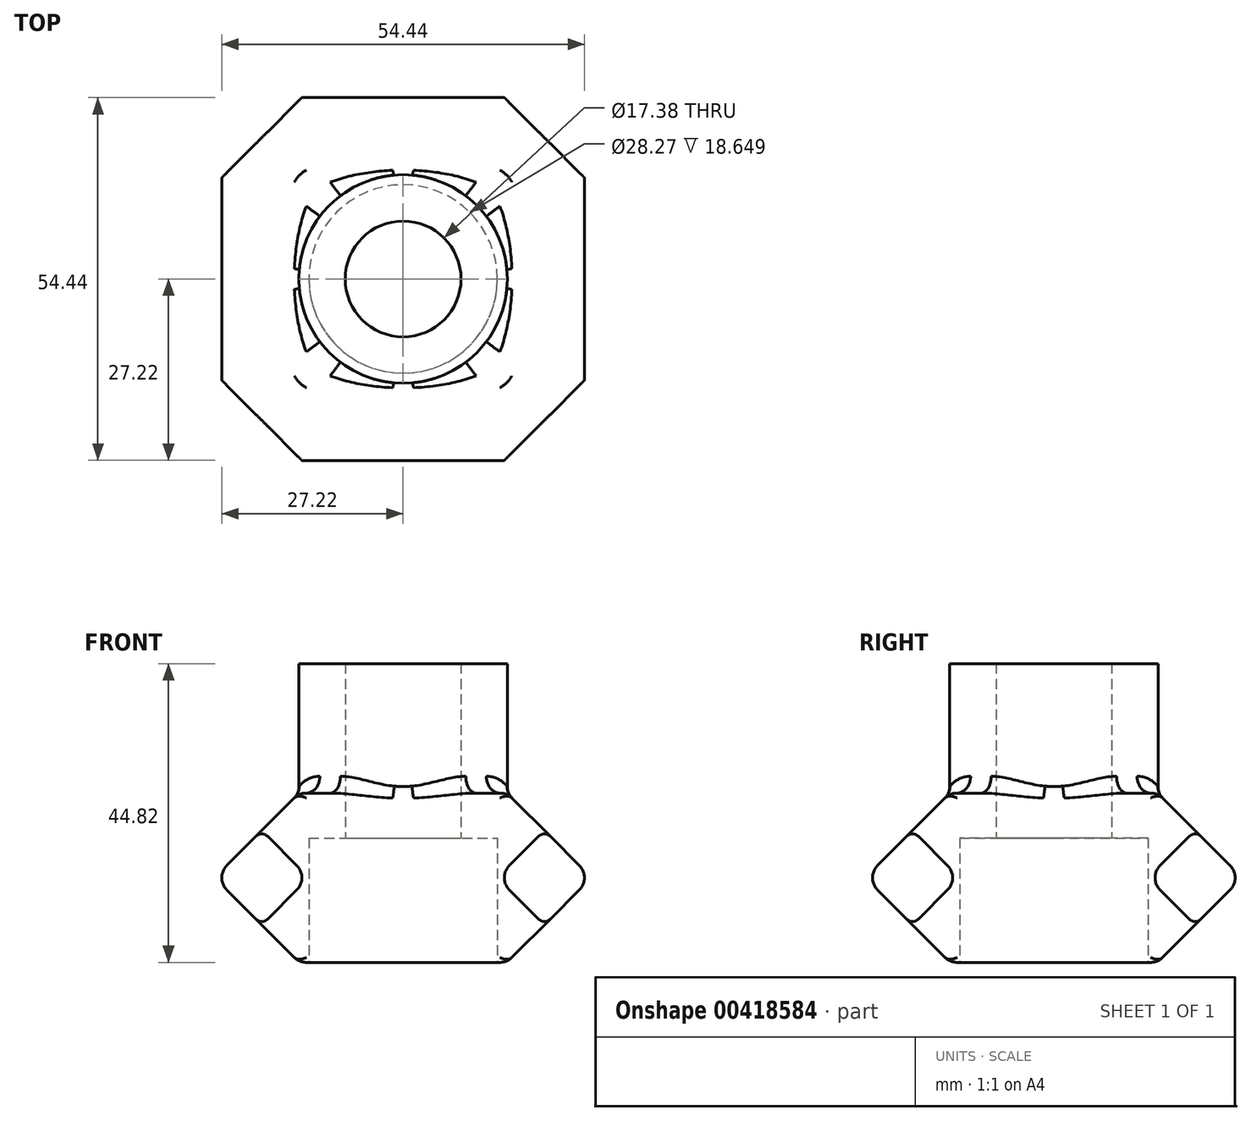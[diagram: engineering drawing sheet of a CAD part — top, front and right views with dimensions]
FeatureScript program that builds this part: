
annotation { "Feature Type Name" : "Feature", "Feature Type Description" : "" }
export const myFeature = defineFeature(function(context is Context, id is Id, definition is map)
    precondition{}
    {
        {
            var Q0;
            Q0=qCreatedBy(makeId("Front.planeOp"),FACE);
            var sketch = newSketch(context, id + "F0", { "sketchPlane" : qUnion([Q0])});
            skLineSegment(sketch, "E0", {"start": v(0, 0) * mm, "end": v(0, 44.82) * mm, "construction": true});
            skLineSegment(sketch, "E1", {"start": v(0, 44.82) * mm, "end": v(15.64, 44.82) * mm, "construction": true});
            skLineSegment(sketch, "E2", {"start": v(15.64, 44.82) * mm, "end": v(15.64, 18.65) * mm});
            skLineSegment(sketch, "E3", {"start": v(8.69, 44.82) * mm, "end": v(8.69, 18.65) * mm});
            skLineSegment(sketch, "E4", {"start": v(8.69, 44.82) * mm, "end": v(15.64, 44.82) * mm});
            skPoint(sketch, "E5.orphan", {"position": v(8.69, 7) * mm});
            skLineSegment(sketch, "E6", {"start": v(8.69, 18.65) * mm, "end": v(15.64, 18.65) * mm});
            skSolve(sketch);
        }
        {
            var Q0;
            {var subQ0=sQuery(id+"F0.wireOp",EDGE,"E2");Q0=makeQuery(id+"F0.imprint","IMPRINT",FACE,{"disambiguationData":[TD([[makeQuery(id+"F0.imprint","IMPRINT",EDGE,{"derivedFrom":subQ0}),-1.0]])]});}
            var Q1;
            Q1=sQuery(id+"F0.wireOp",EDGE,"E0");
            revolve(context, id + "F1", {"entities" : qUnion([Q0]), "axis" : qUnion([Q1]), "revolveType" : RevolveType.FULL});
        }
        {
            var Q0;
            Q0=qCreatedBy(makeId("Top.planeOp"),FACE);
            var sketch = newSketch(context, id + "F2", { "sketchPlane" : qUnion([Q0])});
            skLineSegment(sketch, "E7", {"start": v(0, 0) * mm, "end": v(28.27, 0) * mm, "construction": true});
            skLineSegment(sketch, "E8", {"start": v(0, 0) * mm, "end": v(0, 28.27) * mm, "construction": true});
            skLineSegment(sketch, "E9", {"start": v(0, 0) * mm, "end": v(-28.27, 0) * mm, "construction": true});
            skLineSegment(sketch, "E10", {"start": v(0, 0) * mm, "end": v(0, -28.27) * mm, "construction": true});
            skLineSegment(sketch, "E11", {"start": v(14.14, 0) * mm, "end": v(14.14, -28.27) * mm});
            skLineSegment(sketch, "E12", {"start": v(0, -14.14) * mm, "end": v(28.27, -14.14) * mm});
            skLineSegment(sketch, "E13", {"start": v(-14.14, 0) * mm, "end": v(-14.14, -28.27) * mm});
            skPoint(sketch, "E13.endSnap0", {"position": v(-14.14, 0) * mm});
            skLineSegment(sketch, "E14", {"start": v(-14.14, 0) * mm, "end": v(-14.14, 28.27) * mm});
            skLineSegment(sketch, "E15", {"start": v(14.14, 0) * mm, "end": v(14.14, 28.27) * mm});
            skLineSegment(sketch, "E16", {"start": v(0, 14.14) * mm, "end": v(28.27, 14.14) * mm});
            skLineSegment(sketch, "E17", {"start": v(0, 14.14) * mm, "end": v(-28.27, 14.14) * mm});
            skLineSegment(sketch, "E18", {"start": v(0, -14.14) * mm, "end": v(-28.27, -14.14) * mm});
            skLineSegment(sketch, "E19", {"start": v(28.27, 14.14) * mm, "end": v(28.27, -14.14) * mm});
            skLineSegment(sketch, "E20", {"start": v(14.14, 28.27) * mm, "end": v(-14.14, 28.27) * mm});
            skLineSegment(sketch, "E21", {"start": v(-28.27, 14.14) * mm, "end": v(-28.27, -14.14) * mm});
            skLineSegment(sketch, "E22", {"start": v(-14.14, -28.27) * mm, "end": v(14.14, -28.27) * mm});
            skLineSegment(sketch, "E23", {"start": v(14.14, -28.27) * mm, "end": v(28.27, -14.14) * mm});
            skLineSegment(sketch, "E24", {"start": v(14.14, 28.27) * mm, "end": v(28.27, 14.14) * mm});
            skLineSegment(sketch, "E25", {"start": v(-14.14, 28.27) * mm, "end": v(-28.27, 14.14) * mm});
            skLineSegment(sketch, "E26", {"start": v(-28.27, -14.14) * mm, "end": v(-14.14, -28.27) * mm});
            skCircle(sketch, "E27", {"center": v(0, 0) * mm, "radius": 14.14 * mm});
            skSolve(sketch);
        }
        {
            var Q0;
            {var subQ0=sQuery(id+"F2.wireOp",EDGE,"E26");Q0=makeQuery(id+"F2.imprint","IMPRINT",FACE,{"disambiguationData":[TD([[makeQuery(id+"F2.imprint","IMPRINT",EDGE,{"derivedFrom":subQ0}),1.0]])]});}
            var Q1;
            {var subQ0=sQuery(id+"F2.wireOp",EDGE,"E23");Q1=makeQuery(id+"F2.imprint","IMPRINT",FACE,{"disambiguationData":[TD([[makeQuery(id+"F2.imprint","IMPRINT",EDGE,{"derivedFrom":subQ0}),1.0]])]});}
            var Q2;
            {var subQ0=sQuery(id+"F2.wireOp",EDGE,"E19");Q2=makeQuery(id+"F2.imprint","IMPRINT",FACE,{"disambiguationData":[TD([[makeQuery(id+"F2.imprint","IMPRINT",EDGE,{"derivedFrom":subQ0}),-1.0]])]});}
            var Q3;
            {var subQ5=sQuery(id+"F2.wireOp",EDGE,"E20");Q3=makeQuery(id+"F2.imprint","IMPRINT",FACE,{"disambiguationData":[TD([[makeQuery(id+"F2.imprint","IMPRINT",EDGE,{"derivedFrom":subQ5}),1.0]])]});}
            var Q4;
            {var subQ0=sQuery(id+"F2.wireOp",EDGE,"E25");Q4=makeQuery(id+"F2.imprint","IMPRINT",FACE,{"disambiguationData":[TD([[makeQuery(id+"F2.imprint","IMPRINT",EDGE,{"derivedFrom":subQ0}),1.0]])]});}
            var Q5;
            {var subQ0=sQuery(id+"F2.wireOp",EDGE,"E24");Q5=makeQuery(id+"F2.imprint","IMPRINT",FACE,{"disambiguationData":[TD([[makeQuery(id+"F2.imprint","IMPRINT",EDGE,{"derivedFrom":subQ0}),-1.0]])]});}
            var Q6;
            {var subQ0=sQuery(id+"F2.wireOp",EDGE,"E21");Q6=makeQuery(id+"F2.imprint","IMPRINT",FACE,{"disambiguationData":[TD([[makeQuery(id+"F2.imprint","IMPRINT",EDGE,{"derivedFrom":subQ0}),1.0]])]});}
            var Q7;
            {var subQ1=sQuery(id+"F2.wireOp",EDGE,"E14");var subQ3=sQuery(id+"F2.wireOp",EDGE,"E17");var subQ4=makeQuery(id+"F2.imprint","INTERSECT",VERTEX,{"derivedFrom":[subQ1,subQ3]});Q7=makeQuery(id+"F2.imprint","IMPRINT",FACE,{"disambiguationData":[TD([[makeQuery(id+"F2.imprint","IMPRINT",EDGE,{"disambiguationData":[TD([[subQ4,1.0]])],"derivedFrom":subQ1}),-1.0]])]});}
            var Q8;
            {var subQ1=sQuery(id+"F2.wireOp",EDGE,"E15");var subQ3=sQuery(id+"F2.wireOp",EDGE,"E16");var subQ4=makeQuery(id+"F2.imprint","INTERSECT",VERTEX,{"derivedFrom":[subQ1,subQ3]});Q8=makeQuery(id+"F2.imprint","IMPRINT",FACE,{"disambiguationData":[TD([[makeQuery(id+"F2.imprint","IMPRINT",EDGE,{"disambiguationData":[TD([[subQ4,1.0]])],"derivedFrom":subQ1}),1.0]])]});}
            var Q9;
            {var subQ1=sQuery(id+"F2.wireOp",EDGE,"E11");var subQ3=sQuery(id+"F2.wireOp",EDGE,"E12");var subQ4=makeQuery(id+"F2.imprint","INTERSECT",VERTEX,{"derivedFrom":[subQ1,subQ3]});Q9=makeQuery(id+"F2.imprint","IMPRINT",FACE,{"disambiguationData":[TD([[makeQuery(id+"F2.imprint","IMPRINT",EDGE,{"disambiguationData":[TD([[subQ4,1.0]])],"derivedFrom":subQ1}),-1.0]])]});}
            var Q10;
            {var subQ1=sQuery(id+"F2.wireOp",EDGE,"E13");var subQ3=sQuery(id+"F2.wireOp",EDGE,"E18");var subQ4=makeQuery(id+"F2.imprint","INTERSECT",VERTEX,{"derivedFrom":[subQ1,subQ3]});Q10=makeQuery(id+"F2.imprint","IMPRINT",FACE,{"disambiguationData":[TD([[makeQuery(id+"F2.imprint","IMPRINT",EDGE,{"disambiguationData":[TD([[subQ4,1.0]])],"derivedFrom":subQ1}),1.0]])]});}
            var Q11;
            {var subQ5=sQuery(id+"F2.wireOp",EDGE,"E22");Q11=makeQuery(id+"F2.imprint","IMPRINT",FACE,{"disambiguationData":[TD([[makeQuery(id+"F2.imprint","IMPRINT",EDGE,{"derivedFrom":subQ5}),1.0]])]});}
            extrude(context, id + "F3", {"entities" : qUnion([Q0, Q1, Q2, Q3, Q4, Q5, Q6, Q7, Q8, Q9, Q10, Q11]), "operationType" : NewBodyOperationType.ADD, "depth" : 25.4 * mm});
        }
        {
            var Q0;
            Q0=makeQuery(id+"F3.opExtrude","CAP_EDGE",EDGE,{"disambiguationData":[OSD([sQuery(id+"F2.wireOp",EDGE,"E26")])],"isStart":false});
            var Q1;
            Q1=makeQuery(id+"F3.opExtrude","CAP_EDGE",EDGE,{"disambiguationData":[OSD([sQuery(id+"F2.wireOp",EDGE,"E26")])],"isStart":true});
            var Q2;
            Q2=makeQuery(id+"F3.opExtrude","CAP_EDGE",EDGE,{"disambiguationData":[OSD([sQuery(id+"F2.wireOp",EDGE,"E23")])],"isStart":true});
            var Q3;
            Q3=makeQuery(id+"F3.opExtrude","CAP_EDGE",EDGE,{"disambiguationData":[OSD([sQuery(id+"F2.wireOp",EDGE,"E23")])],"isStart":false});
            var Q4;
            Q4=makeQuery(id+"F3.opExtrude","CAP_EDGE",EDGE,{"disambiguationData":[OSD([sQuery(id+"F2.wireOp",EDGE,"E24")])],"isStart":false});
            var Q5;
            Q5=makeQuery(id+"F3.opExtrude","CAP_EDGE",EDGE,{"disambiguationData":[OSD([sQuery(id+"F2.wireOp",EDGE,"E24")])],"isStart":true});
            var Q6;
            Q6=makeQuery(id+"F3.opExtrude","CAP_EDGE",EDGE,{"disambiguationData":[OSD([sQuery(id+"F2.wireOp",EDGE,"E25")])],"isStart":true});
            var Q7;
            Q7=makeQuery(id+"F3.opExtrude","CAP_EDGE",EDGE,{"disambiguationData":[OSD([sQuery(id+"F2.wireOp",EDGE,"E25")])],"isStart":false});
            chamfer(context, id + "F4", {"entities" : qUnion([Q0, Q1, Q2, Q3, Q4, Q5, Q6, Q7]), "width" : 5.08 * mm, "tangentPropagation" : true});
        }
        {
            var Q0;
            Q0=makeQuery(id+"F3.opExtrude","CAP_EDGE",EDGE,{"disambiguationData":[OSD([sQuery(id+"F2.wireOp",EDGE,"E20")])],"isStart":false});
            var Q1;
            Q1=makeQuery(id+"F3.opExtrude","CAP_EDGE",EDGE,{"disambiguationData":[OSD([sQuery(id+"F2.wireOp",EDGE,"E20")])],"isStart":true});
            var Q2;
            Q2=makeQuery(id+"F3.opExtrude","CAP_EDGE",EDGE,{"disambiguationData":[OSD([sQuery(id+"F2.wireOp",EDGE,"E21")])],"isStart":true});
            var Q3;
            Q3=makeQuery(id+"F3.opExtrude","CAP_EDGE",EDGE,{"disambiguationData":[OSD([sQuery(id+"F2.wireOp",EDGE,"E21")])],"isStart":false});
            var Q4;
            Q4=makeQuery(id+"F3.opExtrude","CAP_EDGE",EDGE,{"disambiguationData":[OSD([sQuery(id+"F2.wireOp",EDGE,"E22")])],"isStart":false});
            var Q5;
            Q5=makeQuery(id+"F3.opExtrude","CAP_EDGE",EDGE,{"disambiguationData":[OSD([sQuery(id+"F2.wireOp",EDGE,"E22")])],"isStart":true});
            var Q6;
            Q6=makeQuery(id+"F3.opExtrude","CAP_EDGE",EDGE,{"disambiguationData":[OSD([sQuery(id+"F2.wireOp",EDGE,"E19")])],"isStart":false});
            var Q7;
            Q7=makeQuery(id+"F3.opExtrude","CAP_EDGE",EDGE,{"disambiguationData":[OSD([sQuery(id+"F2.wireOp",EDGE,"E19")])],"isStart":true});
            chamfer(context, id + "F5", {"entities" : qUnion([Q0, Q1, Q2, Q3, Q4, Q5, Q6, Q7]), "width" : 12.7 * mm, "tangentPropagation" : true});
        }
        {
            var Q0;
            Q0=makeQuery(id+"F5.opChamfer","BLEND_EDGE",EDGE,{"blendedFrom":[makeQuery(id+"F3.opExtrude","CAP_EDGE",EDGE,{"disambiguationData":[OSD([sQuery(id+"F2.wireOp",EDGE,"E20")])],"isStart":false}),makeQuery(id+"F3.opExtrude","CAP_EDGE",EDGE,{"disambiguationData":[OSD([sQuery(id+"F2.wireOp",EDGE,"E21")])],"isStart":false})],"blendedInto":[]});
            var Q1;
            {var subQ0=sQuery(id+"F2.wireOp",EDGE,"E21");Q1=makeQuery(id+"F5.opChamfer","BLEND_EDGE",EDGE,{"disambiguationData":[OD(0.0)],"blendedFrom":[makeQuery(id+"F3.opExtrude","CAP_EDGE",EDGE,{"disambiguationData":[OSD([subQ0])],"isStart":false}),makeQuery(id+"F3.opExtrude","CAP_FACE",FACE,{"disambiguationData":[OSD([sQuery(id+"F2.wireOp",EDGE,"E19"),sQuery(id+"F2.wireOp",EDGE,"E20"),subQ0,sQuery(id+"F2.wireOp",EDGE,"E22"),sQuery(id+"F2.wireOp",EDGE,"E23"),sQuery(id+"F2.wireOp",EDGE,"E24"),sQuery(id+"F2.wireOp",EDGE,"E25"),sQuery(id+"F2.wireOp",EDGE,"E26"),sQuery(id+"F2.wireOp",EDGE,"E27")])],"isStart":false})],"blendedInto":[makeQuery(id+"F3.opExtrude","CAP_FACE",FACE,{"disambiguationData":[OSD([sQuery(id+"F2.wireOp",EDGE,"E19"),sQuery(id+"F2.wireOp",EDGE,"E20"),subQ0,sQuery(id+"F2.wireOp",EDGE,"E22"),sQuery(id+"F2.wireOp",EDGE,"E23"),sQuery(id+"F2.wireOp",EDGE,"E24"),sQuery(id+"F2.wireOp",EDGE,"E25"),sQuery(id+"F2.wireOp",EDGE,"E26"),sQuery(id+"F2.wireOp",EDGE,"E27")])],"isStart":false})]});}
            var Q2;
            {var subQ0=sQuery(id+"F2.wireOp",EDGE,"E20");Q2=makeQuery(id+"F5.opChamfer","BLEND_EDGE",EDGE,{"disambiguationData":[OD(1.0)],"blendedFrom":[makeQuery(id+"F3.opExtrude","CAP_EDGE",EDGE,{"disambiguationData":[OSD([subQ0])],"isStart":false}),makeQuery(id+"F3.opExtrude","CAP_FACE",FACE,{"disambiguationData":[OSD([sQuery(id+"F2.wireOp",EDGE,"E19"),subQ0,sQuery(id+"F2.wireOp",EDGE,"E21"),sQuery(id+"F2.wireOp",EDGE,"E22"),sQuery(id+"F2.wireOp",EDGE,"E23"),sQuery(id+"F2.wireOp",EDGE,"E24"),sQuery(id+"F2.wireOp",EDGE,"E25"),sQuery(id+"F2.wireOp",EDGE,"E26"),sQuery(id+"F2.wireOp",EDGE,"E27")])],"isStart":false})],"blendedInto":[makeQuery(id+"F3.opExtrude","CAP_FACE",FACE,{"disambiguationData":[OSD([sQuery(id+"F2.wireOp",EDGE,"E19"),subQ0,sQuery(id+"F2.wireOp",EDGE,"E21"),sQuery(id+"F2.wireOp",EDGE,"E22"),sQuery(id+"F2.wireOp",EDGE,"E23"),sQuery(id+"F2.wireOp",EDGE,"E24"),sQuery(id+"F2.wireOp",EDGE,"E25"),sQuery(id+"F2.wireOp",EDGE,"E26"),sQuery(id+"F2.wireOp",EDGE,"E27")])],"isStart":false})]});}
            var Q3;
            {var subQ0=sQuery(id+"F2.wireOp",EDGE,"E19");Q3=makeQuery(id+"F5.opChamfer","BLEND_EDGE",EDGE,{"disambiguationData":[OD(0.0)],"blendedFrom":[makeQuery(id+"F3.opExtrude","CAP_EDGE",EDGE,{"disambiguationData":[OSD([subQ0])],"isStart":false}),makeQuery(id+"F3.opExtrude","CAP_FACE",FACE,{"disambiguationData":[OSD([subQ0,sQuery(id+"F2.wireOp",EDGE,"E20"),sQuery(id+"F2.wireOp",EDGE,"E21"),sQuery(id+"F2.wireOp",EDGE,"E22"),sQuery(id+"F2.wireOp",EDGE,"E23"),sQuery(id+"F2.wireOp",EDGE,"E24"),sQuery(id+"F2.wireOp",EDGE,"E25"),sQuery(id+"F2.wireOp",EDGE,"E26"),sQuery(id+"F2.wireOp",EDGE,"E27")])],"isStart":false})],"blendedInto":[makeQuery(id+"F3.opExtrude","CAP_FACE",FACE,{"disambiguationData":[OSD([subQ0,sQuery(id+"F2.wireOp",EDGE,"E20"),sQuery(id+"F2.wireOp",EDGE,"E21"),sQuery(id+"F2.wireOp",EDGE,"E22"),sQuery(id+"F2.wireOp",EDGE,"E23"),sQuery(id+"F2.wireOp",EDGE,"E24"),sQuery(id+"F2.wireOp",EDGE,"E25"),sQuery(id+"F2.wireOp",EDGE,"E26"),sQuery(id+"F2.wireOp",EDGE,"E27")])],"isStart":false})]});}
            var Q4;
            Q4=makeQuery(id+"F5.opChamfer","BLEND_EDGE",EDGE,{"blendedFrom":[makeQuery(id+"F3.opExtrude","CAP_EDGE",EDGE,{"disambiguationData":[OSD([sQuery(id+"F2.wireOp",EDGE,"E19")])],"isStart":false}),makeQuery(id+"F3.opExtrude","CAP_EDGE",EDGE,{"disambiguationData":[OSD([sQuery(id+"F2.wireOp",EDGE,"E20")])],"isStart":false})],"blendedInto":[]});
            var Q5;
            Q5=makeQuery(id+"F5.opChamfer","BLEND_EDGE",EDGE,{"blendedFrom":[makeQuery(id+"F3.opExtrude","CAP_EDGE",EDGE,{"disambiguationData":[OSD([sQuery(id+"F2.wireOp",EDGE,"E19")])],"isStart":false}),makeQuery(id+"F3.opExtrude","CAP_EDGE",EDGE,{"disambiguationData":[OSD([sQuery(id+"F2.wireOp",EDGE,"E22")])],"isStart":false})],"blendedInto":[]});
            var Q6;
            {var subQ0=sQuery(id+"F2.wireOp",EDGE,"E19");Q6=makeQuery(id+"F5.opChamfer","BLEND_EDGE",EDGE,{"disambiguationData":[OD(1.0)],"blendedFrom":[makeQuery(id+"F3.opExtrude","CAP_EDGE",EDGE,{"disambiguationData":[OSD([subQ0])],"isStart":false}),makeQuery(id+"F3.opExtrude","CAP_FACE",FACE,{"disambiguationData":[OSD([subQ0,sQuery(id+"F2.wireOp",EDGE,"E20"),sQuery(id+"F2.wireOp",EDGE,"E21"),sQuery(id+"F2.wireOp",EDGE,"E22"),sQuery(id+"F2.wireOp",EDGE,"E23"),sQuery(id+"F2.wireOp",EDGE,"E24"),sQuery(id+"F2.wireOp",EDGE,"E25"),sQuery(id+"F2.wireOp",EDGE,"E26"),sQuery(id+"F2.wireOp",EDGE,"E27")])],"isStart":false})],"blendedInto":[makeQuery(id+"F3.opExtrude","CAP_FACE",FACE,{"disambiguationData":[OSD([subQ0,sQuery(id+"F2.wireOp",EDGE,"E20"),sQuery(id+"F2.wireOp",EDGE,"E21"),sQuery(id+"F2.wireOp",EDGE,"E22"),sQuery(id+"F2.wireOp",EDGE,"E23"),sQuery(id+"F2.wireOp",EDGE,"E24"),sQuery(id+"F2.wireOp",EDGE,"E25"),sQuery(id+"F2.wireOp",EDGE,"E26"),sQuery(id+"F2.wireOp",EDGE,"E27")])],"isStart":false})]});}
            var Q7;
            Q7=makeQuery(id+"F5.opChamfer","BLEND_EDGE",EDGE,{"blendedFrom":[makeQuery(id+"F3.opExtrude","CAP_EDGE",EDGE,{"disambiguationData":[OSD([sQuery(id+"F2.wireOp",EDGE,"E19")])],"isStart":false}),makeQuery(id+"F1.opRevolve","SWEPT_FACE",FACE,{"disambiguationData":[OSD([sQuery(id+"F0.wireOp",EDGE,"E2")])]})],"blendedInto":[makeQuery(id+"F1.opRevolve","SWEPT_FACE",FACE,{"disambiguationData":[OSD([sQuery(id+"F0.wireOp",EDGE,"E2")])]})]});
            var Q8;
            Q8=makeQuery(id+"F3.boolean.opBoolean","INTERSECT",EDGE,{"derivedFrom":[makeQuery(id+"F1.opRevolve","SWEPT_FACE",FACE,{"disambiguationData":[OSD([sQuery(id+"F0.wireOp",EDGE,"E2")])]}),makeQuery(id+"F3.opExtrude","CAP_FACE",FACE,{"disambiguationData":[OSD([sQuery(id+"F2.wireOp",EDGE,"E19"),sQuery(id+"F2.wireOp",EDGE,"E20"),sQuery(id+"F2.wireOp",EDGE,"E21"),sQuery(id+"F2.wireOp",EDGE,"E22"),sQuery(id+"F2.wireOp",EDGE,"E23"),sQuery(id+"F2.wireOp",EDGE,"E24"),sQuery(id+"F2.wireOp",EDGE,"E25"),sQuery(id+"F2.wireOp",EDGE,"E26"),sQuery(id+"F2.wireOp",EDGE,"E27")])],"isStart":false})]});
            var Q9;
            {var subQ0=sQuery(id+"F2.wireOp",EDGE,"E22");Q9=makeQuery(id+"F5.opChamfer","BLEND_EDGE",EDGE,{"disambiguationData":[OD(0.0)],"blendedFrom":[makeQuery(id+"F3.opExtrude","CAP_EDGE",EDGE,{"disambiguationData":[OSD([subQ0])],"isStart":false}),makeQuery(id+"F3.opExtrude","CAP_FACE",FACE,{"disambiguationData":[OSD([sQuery(id+"F2.wireOp",EDGE,"E19"),sQuery(id+"F2.wireOp",EDGE,"E20"),sQuery(id+"F2.wireOp",EDGE,"E21"),subQ0,sQuery(id+"F2.wireOp",EDGE,"E23"),sQuery(id+"F2.wireOp",EDGE,"E24"),sQuery(id+"F2.wireOp",EDGE,"E25"),sQuery(id+"F2.wireOp",EDGE,"E26"),sQuery(id+"F2.wireOp",EDGE,"E27")])],"isStart":false})],"blendedInto":[makeQuery(id+"F3.opExtrude","CAP_FACE",FACE,{"disambiguationData":[OSD([sQuery(id+"F2.wireOp",EDGE,"E19"),sQuery(id+"F2.wireOp",EDGE,"E20"),sQuery(id+"F2.wireOp",EDGE,"E21"),subQ0,sQuery(id+"F2.wireOp",EDGE,"E23"),sQuery(id+"F2.wireOp",EDGE,"E24"),sQuery(id+"F2.wireOp",EDGE,"E25"),sQuery(id+"F2.wireOp",EDGE,"E26"),sQuery(id+"F2.wireOp",EDGE,"E27")])],"isStart":false})]});}
            var Q10;
            {var subQ0=sQuery(id+"F2.wireOp",EDGE,"E20");Q10=makeQuery(id+"F5.opChamfer","BLEND_EDGE",EDGE,{"disambiguationData":[OD(0.0)],"blendedFrom":[makeQuery(id+"F3.opExtrude","CAP_EDGE",EDGE,{"disambiguationData":[OSD([subQ0])],"isStart":false}),makeQuery(id+"F3.opExtrude","CAP_FACE",FACE,{"disambiguationData":[OSD([sQuery(id+"F2.wireOp",EDGE,"E19"),subQ0,sQuery(id+"F2.wireOp",EDGE,"E21"),sQuery(id+"F2.wireOp",EDGE,"E22"),sQuery(id+"F2.wireOp",EDGE,"E23"),sQuery(id+"F2.wireOp",EDGE,"E24"),sQuery(id+"F2.wireOp",EDGE,"E25"),sQuery(id+"F2.wireOp",EDGE,"E26"),sQuery(id+"F2.wireOp",EDGE,"E27")])],"isStart":false})],"blendedInto":[makeQuery(id+"F3.opExtrude","CAP_FACE",FACE,{"disambiguationData":[OSD([sQuery(id+"F2.wireOp",EDGE,"E19"),subQ0,sQuery(id+"F2.wireOp",EDGE,"E21"),sQuery(id+"F2.wireOp",EDGE,"E22"),sQuery(id+"F2.wireOp",EDGE,"E23"),sQuery(id+"F2.wireOp",EDGE,"E24"),sQuery(id+"F2.wireOp",EDGE,"E25"),sQuery(id+"F2.wireOp",EDGE,"E26"),sQuery(id+"F2.wireOp",EDGE,"E27")])],"isStart":false})]});}
            var Q11;
            {var subQ0=sQuery(id+"F2.wireOp",EDGE,"E22");Q11=makeQuery(id+"F5.opChamfer","BLEND_EDGE",EDGE,{"disambiguationData":[OD(1.0)],"blendedFrom":[makeQuery(id+"F3.opExtrude","CAP_EDGE",EDGE,{"disambiguationData":[OSD([subQ0])],"isStart":false}),makeQuery(id+"F3.opExtrude","CAP_FACE",FACE,{"disambiguationData":[OSD([sQuery(id+"F2.wireOp",EDGE,"E19"),sQuery(id+"F2.wireOp",EDGE,"E20"),sQuery(id+"F2.wireOp",EDGE,"E21"),subQ0,sQuery(id+"F2.wireOp",EDGE,"E23"),sQuery(id+"F2.wireOp",EDGE,"E24"),sQuery(id+"F2.wireOp",EDGE,"E25"),sQuery(id+"F2.wireOp",EDGE,"E26"),sQuery(id+"F2.wireOp",EDGE,"E27")])],"isStart":false})],"blendedInto":[makeQuery(id+"F3.opExtrude","CAP_FACE",FACE,{"disambiguationData":[OSD([sQuery(id+"F2.wireOp",EDGE,"E19"),sQuery(id+"F2.wireOp",EDGE,"E20"),sQuery(id+"F2.wireOp",EDGE,"E21"),subQ0,sQuery(id+"F2.wireOp",EDGE,"E23"),sQuery(id+"F2.wireOp",EDGE,"E24"),sQuery(id+"F2.wireOp",EDGE,"E25"),sQuery(id+"F2.wireOp",EDGE,"E26"),sQuery(id+"F2.wireOp",EDGE,"E27")])],"isStart":false})]});}
            var Q12;
            {var subQ0=sQuery(id+"F2.wireOp",EDGE,"E21");Q12=makeQuery(id+"F5.opChamfer","BLEND_EDGE",EDGE,{"disambiguationData":[OD(1.0)],"blendedFrom":[makeQuery(id+"F3.opExtrude","CAP_EDGE",EDGE,{"disambiguationData":[OSD([subQ0])],"isStart":false}),makeQuery(id+"F3.opExtrude","CAP_FACE",FACE,{"disambiguationData":[OSD([sQuery(id+"F2.wireOp",EDGE,"E19"),sQuery(id+"F2.wireOp",EDGE,"E20"),subQ0,sQuery(id+"F2.wireOp",EDGE,"E22"),sQuery(id+"F2.wireOp",EDGE,"E23"),sQuery(id+"F2.wireOp",EDGE,"E24"),sQuery(id+"F2.wireOp",EDGE,"E25"),sQuery(id+"F2.wireOp",EDGE,"E26"),sQuery(id+"F2.wireOp",EDGE,"E27")])],"isStart":false})],"blendedInto":[makeQuery(id+"F3.opExtrude","CAP_FACE",FACE,{"disambiguationData":[OSD([sQuery(id+"F2.wireOp",EDGE,"E19"),sQuery(id+"F2.wireOp",EDGE,"E20"),subQ0,sQuery(id+"F2.wireOp",EDGE,"E22"),sQuery(id+"F2.wireOp",EDGE,"E23"),sQuery(id+"F2.wireOp",EDGE,"E24"),sQuery(id+"F2.wireOp",EDGE,"E25"),sQuery(id+"F2.wireOp",EDGE,"E26"),sQuery(id+"F2.wireOp",EDGE,"E27")])],"isStart":false})]});}
            var Q13;
            Q13=makeQuery(id+"F5.opChamfer","BLEND_EDGE",EDGE,{"blendedFrom":[makeQuery(id+"F3.opExtrude","CAP_EDGE",EDGE,{"disambiguationData":[OSD([sQuery(id+"F2.wireOp",EDGE,"E22")])],"isStart":false}),makeQuery(id+"F1.opRevolve","SWEPT_FACE",FACE,{"disambiguationData":[OSD([sQuery(id+"F0.wireOp",EDGE,"E2")])]})],"blendedInto":[makeQuery(id+"F1.opRevolve","SWEPT_FACE",FACE,{"disambiguationData":[OSD([sQuery(id+"F0.wireOp",EDGE,"E2")])]})]});
            var Q14;
            Q14=makeQuery(id+"F5.opChamfer","BLEND_EDGE",EDGE,{"blendedFrom":[makeQuery(id+"F3.opExtrude","CAP_EDGE",EDGE,{"disambiguationData":[OSD([sQuery(id+"F2.wireOp",EDGE,"E21")])],"isStart":false}),makeQuery(id+"F3.opExtrude","CAP_EDGE",EDGE,{"disambiguationData":[OSD([sQuery(id+"F2.wireOp",EDGE,"E22")])],"isStart":false})],"blendedInto":[]});
            var Q15;
            Q15=makeQuery(id+"F5.opChamfer","BLEND_EDGE",EDGE,{"blendedFrom":[makeQuery(id+"F3.opExtrude","CAP_EDGE",EDGE,{"disambiguationData":[OSD([sQuery(id+"F2.wireOp",EDGE,"E21")])],"isStart":false}),makeQuery(id+"F1.opRevolve","SWEPT_FACE",FACE,{"disambiguationData":[OSD([sQuery(id+"F0.wireOp",EDGE,"E2")])]})],"blendedInto":[makeQuery(id+"F1.opRevolve","SWEPT_FACE",FACE,{"disambiguationData":[OSD([sQuery(id+"F0.wireOp",EDGE,"E2")])]})]});
            var Q16;
            Q16=makeQuery(id+"F5.opChamfer","BLEND_EDGE",EDGE,{"blendedFrom":[makeQuery(id+"F3.opExtrude","CAP_EDGE",EDGE,{"disambiguationData":[OSD([sQuery(id+"F2.wireOp",EDGE,"E20")])],"isStart":false}),makeQuery(id+"F1.opRevolve","SWEPT_FACE",FACE,{"disambiguationData":[OSD([sQuery(id+"F0.wireOp",EDGE,"E2")])]})],"blendedInto":[makeQuery(id+"F1.opRevolve","SWEPT_FACE",FACE,{"disambiguationData":[OSD([sQuery(id+"F0.wireOp",EDGE,"E2")])]})]});
            var Q17;
            {var subQ0=sQuery(id+"F2.wireOp",EDGE,"E21");Q17=makeQuery(id+"F5.opChamfer","BLEND_EDGE",EDGE,{"blendedFrom":[makeQuery(id+"F3.opExtrude","CAP_EDGE",EDGE,{"disambiguationData":[OSD([subQ0])],"isStart":true}),makeQuery(id+"F3.opExtrude","CAP_EDGE",EDGE,{"disambiguationData":[OSD([subQ0])],"isStart":false})],"blendedInto":[]});}
            var Q18;
            {var subQ0=sQuery(id+"F2.wireOp",EDGE,"E20");Q18=makeQuery(id+"F5.opChamfer","BLEND_EDGE",EDGE,{"blendedFrom":[makeQuery(id+"F3.opExtrude","CAP_EDGE",EDGE,{"disambiguationData":[OSD([subQ0])],"isStart":true}),makeQuery(id+"F3.opExtrude","CAP_EDGE",EDGE,{"disambiguationData":[OSD([subQ0])],"isStart":false})],"blendedInto":[]});}
            var Q19;
            {var subQ0=sQuery(id+"F2.wireOp",EDGE,"E19");Q19=makeQuery(id+"F5.opChamfer","BLEND_EDGE",EDGE,{"blendedFrom":[makeQuery(id+"F3.opExtrude","CAP_EDGE",EDGE,{"disambiguationData":[OSD([subQ0])],"isStart":true}),makeQuery(id+"F3.opExtrude","CAP_EDGE",EDGE,{"disambiguationData":[OSD([subQ0])],"isStart":false})],"blendedInto":[]});}
            var Q20;
            {var subQ0=sQuery(id+"F2.wireOp",EDGE,"E22");Q20=makeQuery(id+"F5.opChamfer","BLEND_EDGE",EDGE,{"blendedFrom":[makeQuery(id+"F3.opExtrude","CAP_EDGE",EDGE,{"disambiguationData":[OSD([subQ0])],"isStart":true}),makeQuery(id+"F3.opExtrude","CAP_EDGE",EDGE,{"disambiguationData":[OSD([subQ0])],"isStart":false})],"blendedInto":[]});}
            var Q21;
            Q21=makeQuery(id+"F5.opChamfer","BLEND_EDGE",EDGE,{"blendedFrom":[makeQuery(id+"F3.opExtrude","CAP_EDGE",EDGE,{"disambiguationData":[OSD([sQuery(id+"F2.wireOp",EDGE,"E21")])],"isStart":true}),makeQuery(id+"F3.opExtrude","CAP_EDGE",EDGE,{"disambiguationData":[OSD([sQuery(id+"F2.wireOp",EDGE,"E22")])],"isStart":true})],"blendedInto":[]});
            var Q22;
            {var subQ0=sQuery(id+"F2.wireOp",EDGE,"E22");Q22=makeQuery(id+"F5.opChamfer","BLEND_EDGE",EDGE,{"blendedFrom":[makeQuery(id+"F3.opExtrude","CAP_EDGE",EDGE,{"disambiguationData":[OSD([subQ0])],"isStart":true}),makeQuery(id+"F3.opExtrude","CAP_FACE",FACE,{"disambiguationData":[OSD([sQuery(id+"F2.wireOp",EDGE,"E19"),sQuery(id+"F2.wireOp",EDGE,"E20"),sQuery(id+"F2.wireOp",EDGE,"E21"),subQ0,sQuery(id+"F2.wireOp",EDGE,"E23"),sQuery(id+"F2.wireOp",EDGE,"E24"),sQuery(id+"F2.wireOp",EDGE,"E25"),sQuery(id+"F2.wireOp",EDGE,"E26"),sQuery(id+"F2.wireOp",EDGE,"E27")])],"isStart":true})],"blendedInto":[makeQuery(id+"F3.opExtrude","CAP_FACE",FACE,{"disambiguationData":[OSD([sQuery(id+"F2.wireOp",EDGE,"E19"),sQuery(id+"F2.wireOp",EDGE,"E20"),sQuery(id+"F2.wireOp",EDGE,"E21"),subQ0,sQuery(id+"F2.wireOp",EDGE,"E23"),sQuery(id+"F2.wireOp",EDGE,"E24"),sQuery(id+"F2.wireOp",EDGE,"E25"),sQuery(id+"F2.wireOp",EDGE,"E26"),sQuery(id+"F2.wireOp",EDGE,"E27")])],"isStart":true})]});}
            var Q23;
            {var subQ0=sQuery(id+"F2.wireOp",EDGE,"E21");Q23=makeQuery(id+"F5.opChamfer","BLEND_EDGE",EDGE,{"blendedFrom":[makeQuery(id+"F3.opExtrude","CAP_EDGE",EDGE,{"disambiguationData":[OSD([subQ0])],"isStart":true}),makeQuery(id+"F3.opExtrude","CAP_FACE",FACE,{"disambiguationData":[OSD([sQuery(id+"F2.wireOp",EDGE,"E19"),sQuery(id+"F2.wireOp",EDGE,"E20"),subQ0,sQuery(id+"F2.wireOp",EDGE,"E22"),sQuery(id+"F2.wireOp",EDGE,"E23"),sQuery(id+"F2.wireOp",EDGE,"E24"),sQuery(id+"F2.wireOp",EDGE,"E25"),sQuery(id+"F2.wireOp",EDGE,"E26"),sQuery(id+"F2.wireOp",EDGE,"E27")])],"isStart":true})],"blendedInto":[makeQuery(id+"F3.opExtrude","CAP_FACE",FACE,{"disambiguationData":[OSD([sQuery(id+"F2.wireOp",EDGE,"E19"),sQuery(id+"F2.wireOp",EDGE,"E20"),subQ0,sQuery(id+"F2.wireOp",EDGE,"E22"),sQuery(id+"F2.wireOp",EDGE,"E23"),sQuery(id+"F2.wireOp",EDGE,"E24"),sQuery(id+"F2.wireOp",EDGE,"E25"),sQuery(id+"F2.wireOp",EDGE,"E26"),sQuery(id+"F2.wireOp",EDGE,"E27")])],"isStart":true})]});}
            var Q24;
            {var subQ0=sQuery(id+"F2.wireOp",EDGE,"E20");Q24=makeQuery(id+"F5.opChamfer","BLEND_EDGE",EDGE,{"blendedFrom":[makeQuery(id+"F3.opExtrude","CAP_EDGE",EDGE,{"disambiguationData":[OSD([subQ0])],"isStart":true}),makeQuery(id+"F3.opExtrude","CAP_FACE",FACE,{"disambiguationData":[OSD([sQuery(id+"F2.wireOp",EDGE,"E19"),subQ0,sQuery(id+"F2.wireOp",EDGE,"E21"),sQuery(id+"F2.wireOp",EDGE,"E22"),sQuery(id+"F2.wireOp",EDGE,"E23"),sQuery(id+"F2.wireOp",EDGE,"E24"),sQuery(id+"F2.wireOp",EDGE,"E25"),sQuery(id+"F2.wireOp",EDGE,"E26"),sQuery(id+"F2.wireOp",EDGE,"E27")])],"isStart":true})],"blendedInto":[makeQuery(id+"F3.opExtrude","CAP_FACE",FACE,{"disambiguationData":[OSD([sQuery(id+"F2.wireOp",EDGE,"E19"),subQ0,sQuery(id+"F2.wireOp",EDGE,"E21"),sQuery(id+"F2.wireOp",EDGE,"E22"),sQuery(id+"F2.wireOp",EDGE,"E23"),sQuery(id+"F2.wireOp",EDGE,"E24"),sQuery(id+"F2.wireOp",EDGE,"E25"),sQuery(id+"F2.wireOp",EDGE,"E26"),sQuery(id+"F2.wireOp",EDGE,"E27")])],"isStart":true})]});}
            var Q25;
            {var subQ0=sQuery(id+"F2.wireOp",EDGE,"E19");Q25=makeQuery(id+"F5.opChamfer","BLEND_EDGE",EDGE,{"blendedFrom":[makeQuery(id+"F3.opExtrude","CAP_EDGE",EDGE,{"disambiguationData":[OSD([subQ0])],"isStart":true}),makeQuery(id+"F3.opExtrude","CAP_FACE",FACE,{"disambiguationData":[OSD([subQ0,sQuery(id+"F2.wireOp",EDGE,"E20"),sQuery(id+"F2.wireOp",EDGE,"E21"),sQuery(id+"F2.wireOp",EDGE,"E22"),sQuery(id+"F2.wireOp",EDGE,"E23"),sQuery(id+"F2.wireOp",EDGE,"E24"),sQuery(id+"F2.wireOp",EDGE,"E25"),sQuery(id+"F2.wireOp",EDGE,"E26"),sQuery(id+"F2.wireOp",EDGE,"E27")])],"isStart":true})],"blendedInto":[makeQuery(id+"F3.opExtrude","CAP_FACE",FACE,{"disambiguationData":[OSD([subQ0,sQuery(id+"F2.wireOp",EDGE,"E20"),sQuery(id+"F2.wireOp",EDGE,"E21"),sQuery(id+"F2.wireOp",EDGE,"E22"),sQuery(id+"F2.wireOp",EDGE,"E23"),sQuery(id+"F2.wireOp",EDGE,"E24"),sQuery(id+"F2.wireOp",EDGE,"E25"),sQuery(id+"F2.wireOp",EDGE,"E26"),sQuery(id+"F2.wireOp",EDGE,"E27")])],"isStart":true})]});}
            var Q26;
            Q26=makeQuery(id+"F5.opChamfer","BLEND_EDGE",EDGE,{"blendedFrom":[makeQuery(id+"F3.opExtrude","CAP_EDGE",EDGE,{"disambiguationData":[OSD([sQuery(id+"F2.wireOp",EDGE,"E20")])],"isStart":true}),makeQuery(id+"F3.opExtrude","CAP_EDGE",EDGE,{"disambiguationData":[OSD([sQuery(id+"F2.wireOp",EDGE,"E21")])],"isStart":true})],"blendedInto":[]});
            var Q27;
            Q27=makeQuery(id+"F5.opChamfer","BLEND_EDGE",EDGE,{"blendedFrom":[makeQuery(id+"F3.opExtrude","CAP_EDGE",EDGE,{"disambiguationData":[OSD([sQuery(id+"F2.wireOp",EDGE,"E19")])],"isStart":true}),makeQuery(id+"F3.opExtrude","CAP_EDGE",EDGE,{"disambiguationData":[OSD([sQuery(id+"F2.wireOp",EDGE,"E20")])],"isStart":true})],"blendedInto":[]});
            var Q28;
            Q28=makeQuery(id+"F5.opChamfer","BLEND_EDGE",EDGE,{"blendedFrom":[makeQuery(id+"F3.opExtrude","CAP_EDGE",EDGE,{"disambiguationData":[OSD([sQuery(id+"F2.wireOp",EDGE,"E19")])],"isStart":true}),makeQuery(id+"F3.opExtrude","CAP_EDGE",EDGE,{"disambiguationData":[OSD([sQuery(id+"F2.wireOp",EDGE,"E22")])],"isStart":true})],"blendedInto":[]});
            fillet(context, id + "F6", {"entities" : qUnion([Q0, Q1, Q2, Q3, Q4, Q5, Q6, Q7, Q8, Q9, Q10, Q11, Q12, Q13, Q14, Q15, Q16, Q17, Q18, Q19, Q20, Q21, Q22, Q23, Q24, Q25, Q26, Q27, Q28]), "radius" : 2.54 * mm, "tangentPropagation" : true, "allowEdgeOverflow" : false});
        }
    });
